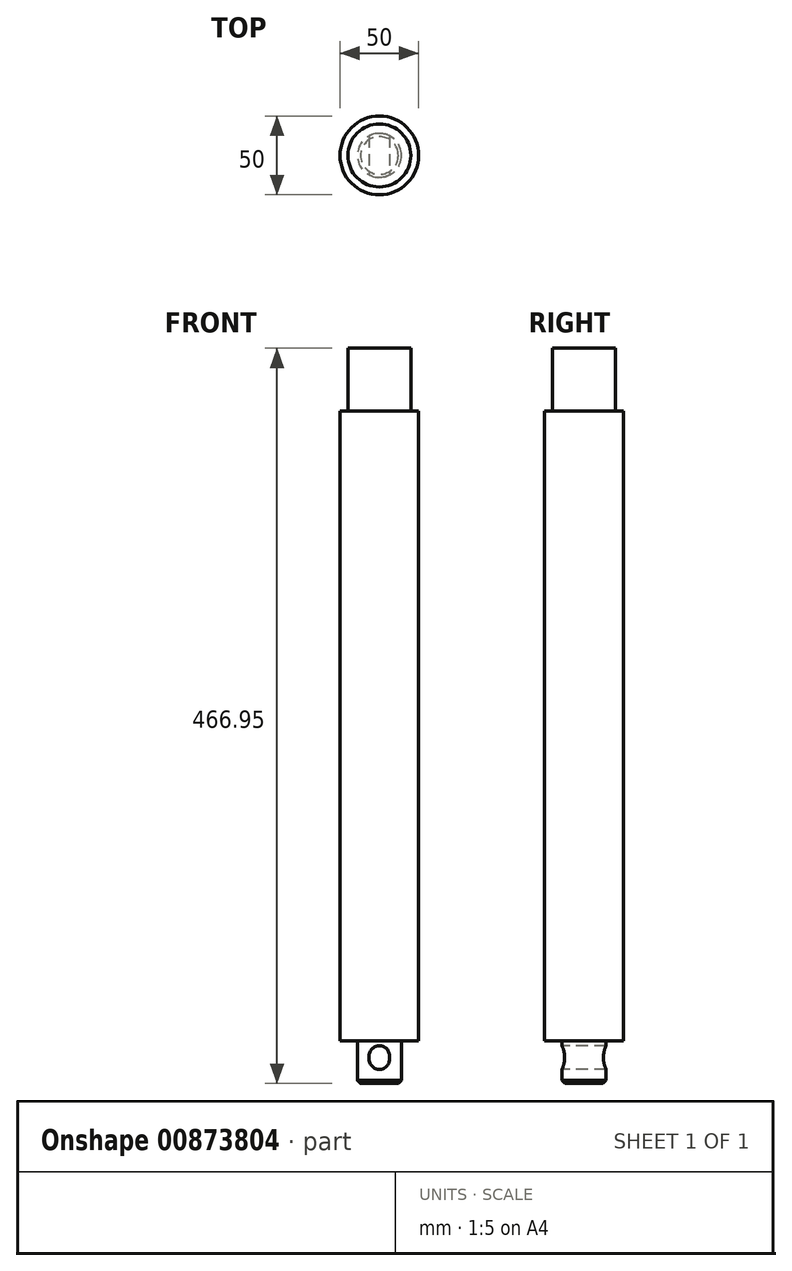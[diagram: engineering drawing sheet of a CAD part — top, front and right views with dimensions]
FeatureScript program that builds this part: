
annotation { "Feature Type Name" : "Feature", "Feature Type Description" : "" }
export const myFeature = defineFeature(function(context is Context, id is Id, definition is map)
    precondition{}
    {
        {
            var Q0;
            Q0=qCreatedBy(makeId("Top.planeOp"),FACE);
            var sketch = newSketch(context, id + "F0", { "sketchPlane" : qUnion([Q0])});
            skCircle(sketch, "E0", {"center": v(0, 0) * mm, "radius": 25 * mm});
            skSolve(sketch);
        }
        {
            var Q0;
            Q0 = qSketchRegion(id + "F0", true);
            extrude(context, id + "F1", {"entities" : qUnion([Q0]), "endBound" : BoundingType.SYMMETRIC, "depth" : 400 * mm, "offsetDistance" : 25 * mm});
        }
        {
            var Q0;
            Q0=makeQuery(id+"F1.opExtrude","CAP_FACE",FACE,{"disambiguationData":[OSD([sQuery(id+"F0.wireOp",EDGE,"E0")])],"isStart":false});
            var sketch = newSketch(context, id + "F2", { "sketchPlane" : qUnion([Q0])});
            skCircle(sketch, "E1", {"center": v(0, 0) * mm, "radius": 20 * mm});
            skSolve(sketch);
        }
        {
            var Q0;
            Q0=makeQuery(id+"F2.imprint","IMPRINT",FACE,{"disambiguationData":[TD([[makeQuery(id+"F2.imprint","IMPRINT",EDGE,{"derivedFrom":sQuery(id+"F2.wireOp",EDGE,"E1")}),1.0]])]});
            extrude(context, id + "F3", {"entities" : qUnion([Q0]), "operationType" : NewBodyOperationType.ADD, "depth" : 40 * mm, "offsetDistance" : 25 * mm});
        }
        {
            var Q0;
            Q0=makeQuery(id+"F1.opExtrude","CAP_FACE",FACE,{"disambiguationData":[OSD([sQuery(id+"F0.wireOp",EDGE,"E0")])],"isStart":true});
            var sketch = newSketch(context, id + "F4", { "sketchPlane" : qUnion([Q0])});
            skCircle(sketch, "E2", {"center": v(0, 0) * mm, "radius": 14 * mm});
            skSolve(sketch);
        }
        {
            var Q0;
            Q0 = qSketchRegion(id + "F4", true);
            extrude(context, id + "F5", {"entities" : qUnion([Q0]), "operationType" : NewBodyOperationType.ADD, "depth" : 26.95 * mm, "offsetDistance" : 25 * mm});
        }
        {
            var Q0;
            Q0=qCreatedBy(makeId("Front.planeOp"),FACE);
            var sketch = newSketch(context, id + "F6", { "sketchPlane" : qUnion([Q0])});
            skLineSegment(sketch, "E3", {"start": v(0, -209.5) * mm, "end": v(0, -211.5) * mm});
            skPoint(sketch, "E4", {"position": v(0, -210.5) * mm});
            skArc(sketch, "E5.0.startCap", {"start": v(-6.5, -209.5) * mm, "mid": v(0, -203) * mm, "end": v(6.5, -209.5) * mm});
            skArc(sketch, "E5.0.endCap", {"start": v(6.5, -211.5) * mm, "mid": v(0, -218) * mm, "end": v(-6.5, -211.5) * mm});
            skLineSegment(sketch, "E5.0.left", {"start": v(6.5, -209.5) * mm, "end": v(6.5, -211.5) * mm});
            skLineSegment(sketch, "E5.0.right", {"start": v(-6.5, -209.5) * mm, "end": v(-6.5, -211.5) * mm});
            skSolve(sketch);
        }
        {
            var Q0;
            Q0 = qSketchRegion(id + "F6", true);
            extrude(context, id + "F7", {"entities" : qUnion([Q0]), "operationType" : NewBodyOperationType.REMOVE, "endBound" : BoundingType.SYMMETRIC, "oppositeDirection" : true, "depth" : 50 * mm, "offsetDistance" : 25 * mm});
        }
        {
            var Q0;
            Q0=makeQuery(id+"F5.opExtrude","CAP_EDGE",EDGE,{"disambiguationData":[OSD([sQuery(id+"F4.wireOp",EDGE,"E2")])],"isStart":false});
            chamfer(context, id + "F8", {"entities" : qUnion([Q0]), "width" : 2 * mm, "tangentPropagation" : true});
        }
    });
